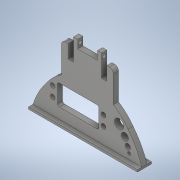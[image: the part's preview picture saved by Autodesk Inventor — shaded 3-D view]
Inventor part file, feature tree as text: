
AUTODESK INVENTOR PART (.ipt)
format: ipt  version: 2020 (Build 240168000, 168)  size: 320,512 bytes
history: mixed  units: mm
features: extrude x6, sketch x6, other x2, imported_body x1
ambient origin geometry x8: Origin, YZ Plane, XZ Plane, XY Plane, X Axis, Y Axis, Z Axis, Center Point
bodies: Body1 (imported_parasolid)
feature tree (15):
  other  "Твердое тело1"
  extrude  "Выдавливание1"  Depth=10.0mm TaperAngle=0.0deg
  extrude  "Выдавливание3"  Depth=13.0mm
  extrude  "Выдавливание4"  Depth=5.0mm
  extrude  "Выдавливание5"  Depth=2.0mm TaperAngle=0.0deg
  extrude  "Выдавливание6"  Depth=30.0mm
  extrude  "Выдавливание7"  Depth=50.0mm
  sketch  "Эскиз1"
  sketch  "Эскиз3"
  sketch  "Эскиз5"
  sketch  "Эскиз6"
  sketch  "Эскиз7"
  sketch  "Эскиз8"
  other  "Cortar-Extruir6"
  imported_body  NMx_Import_Brep_tag  [imported B-rep: ~49 faces, bbox_mm=[105.0, 78.0, 13.48]]
